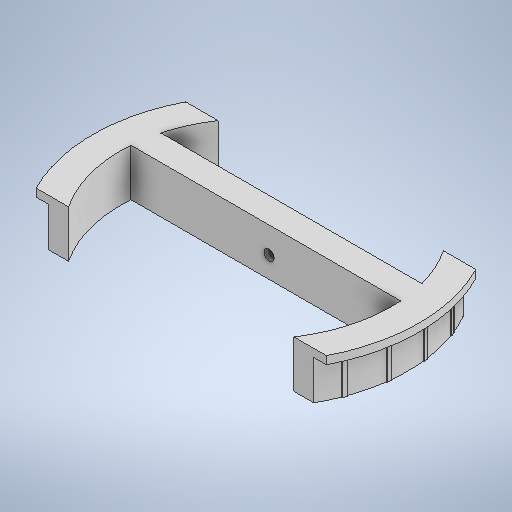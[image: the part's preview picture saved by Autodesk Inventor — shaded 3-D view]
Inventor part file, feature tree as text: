
AUTODESK INVENTOR PART (.ipt)
format: ipt  version: 2025 (Build 290162010, 162A)  size: 756,736 bytes
history: native  units: in
note: dims shown in document units (in); Inventor stores cm internally (conversion verified against a paired STEP export)
features: sketch x4, extrude x2, hole x1
ambient origin geometry x8: Origin, YZ Plane, XZ Plane, XY Plane, X Axis, Y Axis, Z Axis, Center Point
bodies: Solid1 (feature_tree)
feature tree (7):
  extrude  "Extrusion1"  Depth=0.0984in
  extrude  "Extrusion2"  Depth=0.0394in
  hole  "Hole1"  [1 undecoded]
  sketch  "Sketch1"  dims[d0=3.0433in d1=0.1679in d2=0.0984in]
  sketch  "Sketch Circular Pattern2"  dims[d3=0.1378in d10=0.0394in]
  sketch  "Sketch2"  dims[d11=0.0157in d12=10.2362in d14=360.0deg]
  sketch  "Sketch3"  dims[d16=0.5118in d17=0.8465in d18=1.5217in d19=0.1967in d20=0.3937in d21=0.0in d22=3.2677in d23=0.1181in d24=1.6339in d25=0.2559in d26=0.0787in d27=0.0in d28=0.26in d29=1.3827in d30=0.104in d31=0.17in d32=0.1575in d33=0.0787in d34=90.0deg d35=0.4322in d36=0.0in]
note: 1 required parameter value undecoded (feature->parameter linkage not recoverable at this tier; creation-order binding heuristic only, values carry confidence <= 0.55)
